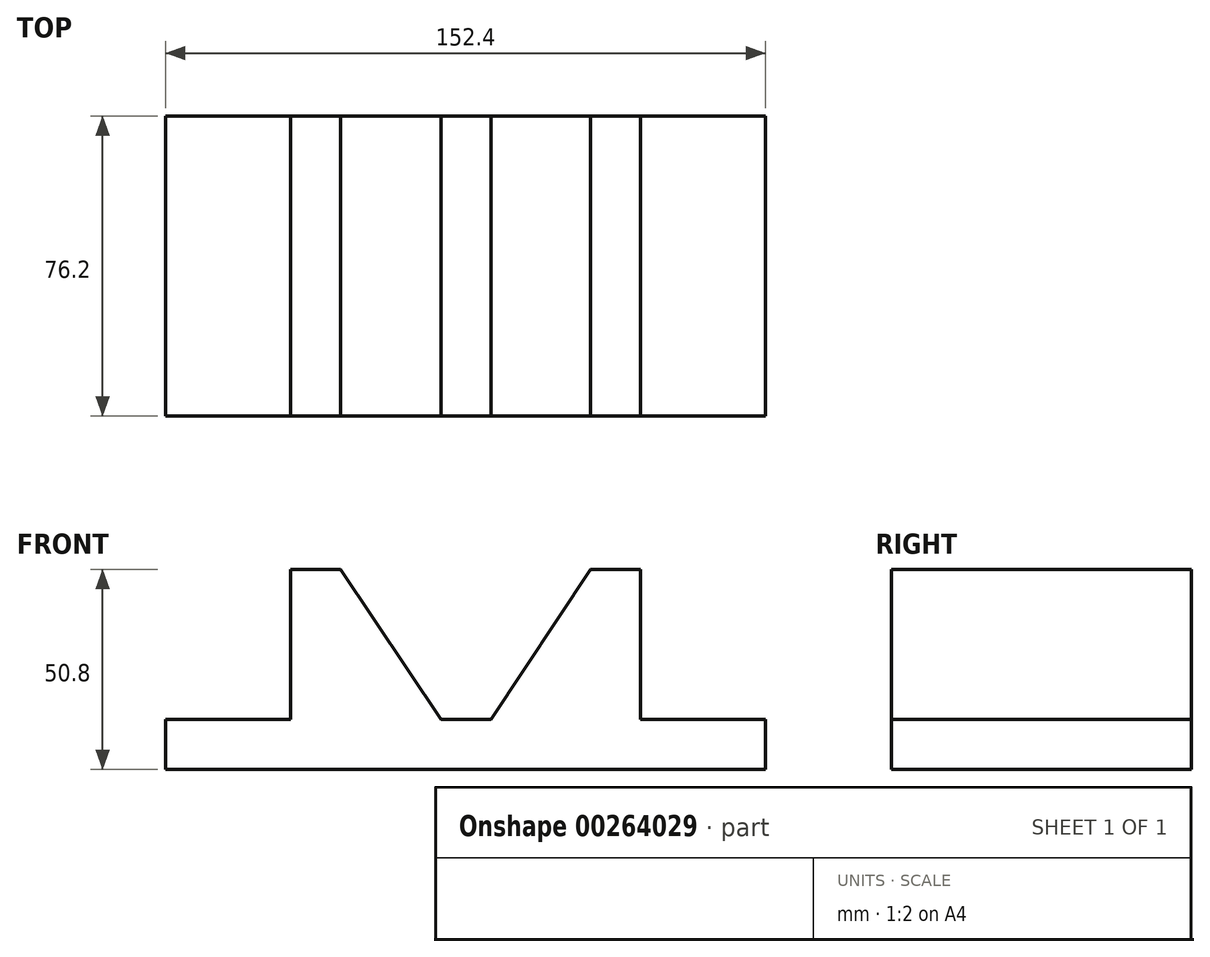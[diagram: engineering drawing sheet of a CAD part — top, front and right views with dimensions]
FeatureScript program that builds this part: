
annotation { "Feature Type Name" : "Feature", "Feature Type Description" : "" }
export const myFeature = defineFeature(function(context is Context, id is Id, definition is map)
    precondition{}
    {
        {
            var Q0;
            Q0=qCreatedBy(makeId("Front.planeOp"),FACE);
            var sketch = newSketch(context, id + "F0", { "sketchPlane" : qUnion([Q0])});
            skPoint(sketch, "E0.start.orphan", {"position": v(-76.56, 0) * mm});
            skLineSegment(sketch, "E1", {"start": v(-76.56, 0) * mm, "end": v(75.84, 0) * mm});
            skLineSegment(sketch, "E2", {"start": v(-76.56, 0) * mm, "end": v(-76.56, 12.7) * mm});
            skLineSegment(sketch, "E3", {"start": v(-76.56, 12.7) * mm, "end": v(-44.8, 12.7) * mm});
            skLineSegment(sketch, "E4", {"start": v(-44.8, 12.7) * mm, "end": v(-44.8, 50.8) * mm});
            skLineSegment(sketch, "E5", {"start": v(-44.8, 50.8) * mm, "end": v(-32.1, 50.8) * mm});
            skLineSegment(sketch, "E6", {"start": v(-32.1, 50.8) * mm, "end": v(-6.62, 12.7) * mm});
            skLineSegment(sketch, "E7", {"start": v(-6.62, 12.7) * mm, "end": v(6.08, 12.7) * mm});
            skLineSegment(sketch, "E8", {"start": v(6.08, 12.7) * mm, "end": v(31.37, 50.8) * mm});
            skLineSegment(sketch, "E9", {"start": v(31.37, 50.8) * mm, "end": v(44.07, 50.8) * mm});
            skLineSegment(sketch, "E10", {"start": v(44.07, 50.8) * mm, "end": v(44.07, 12.7) * mm});
            skLineSegment(sketch, "E11", {"start": v(44.07, 12.7) * mm, "end": v(75.82, 12.7) * mm});
            skLineSegment(sketch, "E12", {"start": v(75.84, 0) * mm, "end": v(75.82, 12.7) * mm});
            skSolve(sketch);
        }
        {
            var Q0;
            Q0=makeQuery(id+"F0.imprint","IMPRINT",FACE,{"disambiguationData":[TD([[makeQuery(id+"F0.imprint","IMPRINT",EDGE,{"derivedFrom":sQuery(id+"F0.wireOp",EDGE,"E1")}),1.0]])]});
            extrude(context, id + "F1", {"entities" : qUnion([Q0]), "depth" : 76.2 * mm});
        }
    });
